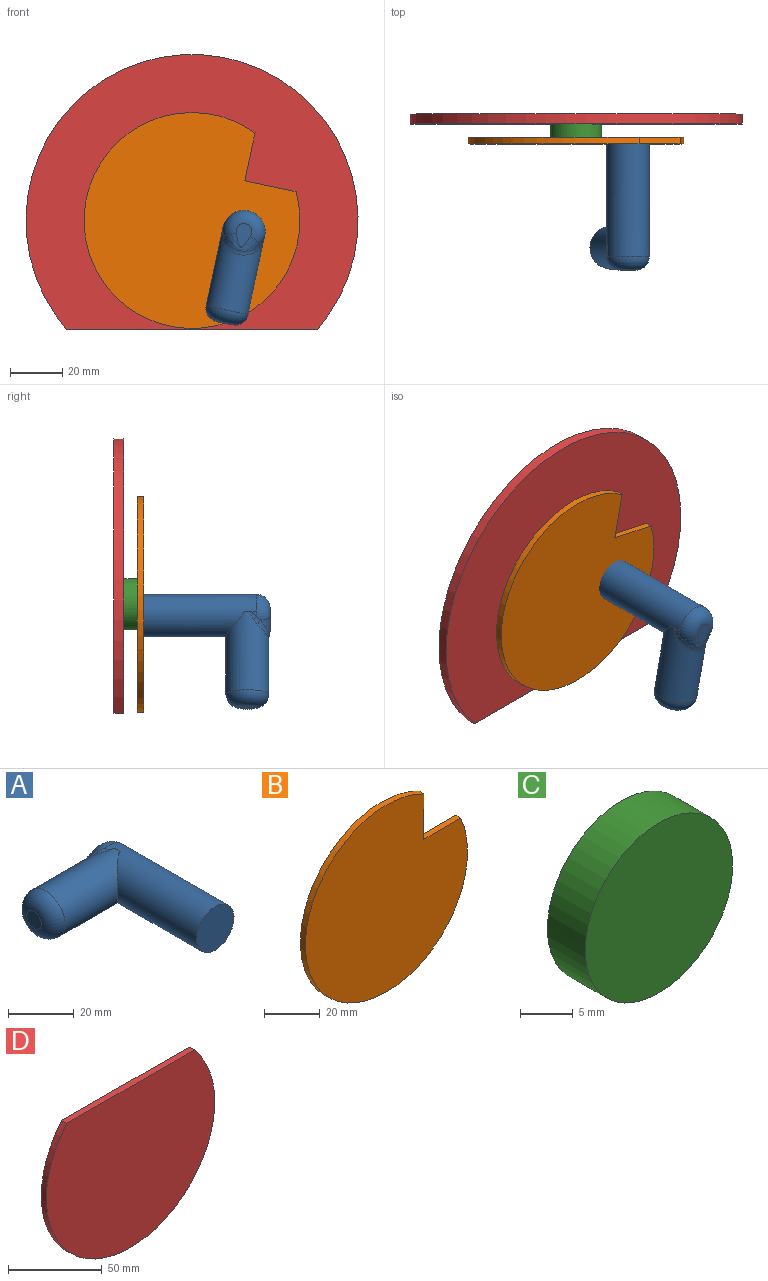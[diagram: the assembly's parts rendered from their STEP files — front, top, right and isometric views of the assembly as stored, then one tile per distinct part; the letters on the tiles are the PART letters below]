
ASSEMBLY  parts=4 mates=3
PART A: 15 faces, bbox 43.9x50.8x16.6 mm
  f0: cylinder r=8.11mm len=45.72mm, axis (0,1,0), area 2104.7mm2, adj f1,f2,f4,f5,f6,f8,f10
  f1: cylinder r=8.11mm len=1.94mm, axis (0,1,0), area 1.9mm2, adj f0,f8,f13
  f2: plane 16.22x16.22mm, normal (0,-1,0), area 206.6mm2, adj f0
  f3: plane 9.11x6.06mm, normal (0,1,0), area 37.8mm2, adj f8,f9
  f4: cylinder r=8.21mm len=30.73mm, axis (1,0,0), area 1303mm2, adj f0,f5,f6,f10,f11,f12,f13,f14
  f5: plane 2.95x0.1mm, normal (1,0,0), area 0.2mm2, adj f0,f4,f13
  f6: plane 2.6x0.1mm, normal (1,0,0), area 0.2mm2, adj f0,f4
  f7: plane 6.27x6.27mm, normal (-1,0,0), area 30.8mm2, adj f14
  f8: torus R=3.03mm, axis (0,-1,0), area 197.1mm2, adj f0,f1,f3,f9,f10,f12
  f9: bspline ~16.11x7.7mm, area 56.5mm2, adj f3,f8,f11
  f10: bspline ~5.46x3.81mm, area 6.8mm2, adj f0,f4,f8,f11
  f11: bspline ~15.04x6.45mm, area 32.1mm2, adj f4,f9,f10,f12
  f12: bspline ~4.32x3.68mm, area 4.8mm2, adj f4,f8,f11,f13
  f13: bspline ~4.16x3.21mm, area 3.5mm2, adj f1,f4,f5,f12
  f14: torus R=3.13mm, axis (1,0,0), area 319.2mm2, adj f4,f7
PART B: 5 faces, bbox 82.5x2.5x82.5 mm
  f0: plane 82.55x82.55mm, normal (0,1,0), area 5121.1mm2, adj f1,f3,f4
  f1: cylinder r=41.27mm len=82.55mm, axis (0,1,0), area 587.7mm2, adj f0,f2,f3,f4
  f2: plane 82.55x82.55mm, normal (0,-1,0), area 5121.1mm2, adj f1,f3,f4
  f3: plane 20.01x2.54mm, normal (1,0,0), area 50.8mm2, adj f0,f1,f2,f4
  f4: plane 18.72x2.54mm, normal (0,0,1), area 47.5mm2, adj f0,f1,f2,f3
PART C: 3 faces, bbox 19.8x5.1x19.8 mm
  f0: cylinder r=9.88mm len=19.76mm, axis (0,1,0), area 315.4mm2, adj f1,f2
  f1: plane 19.76x19.76mm, normal (0,-1,0), area 306.7mm2, adj f0
  f2: plane 19.76x19.76mm, normal (0,1,0), area 306.7mm2, adj f0
PART D: 4 faces, bbox 127x3.8x105.1 mm
  f0: cylinder r=63.5mm len=127mm, axis (0,1,0), area 1105.5mm2, adj f1,f2,f3
  f1: plane 127x105.08mm, normal (0,-1,0), area 11207.7mm2, adj f0,f3
  f2: plane 127x105.08mm, normal (0,1,0), area 11207.7mm2, adj f0,f3
  f3: plane 95.99x3.81mm, normal (0,0,1), area 365.7mm2, adj f0,f1,f2
PLACE A rot(axis=(0.78,0,0.63),180deg) t=(32.76,-45.43,54.32)mm
PLACE B rot(axis=(0.78,0,0.63),180deg) t=(12.89,2.83,58.56)mm
PLACE C rot(axis=(0,-1,0),180deg) t=(12.89,10.45,58.56)mm
PLACE D rot(axis=(0,-1,0),180deg) t=(12.89,14.26,58.56)mm fixed
MATE fastened C.f0 <-> D.f0  axis (0,1,0) through (12.89,10.45,58.56)mm
MATE revolute B.f1 <-> C.f0  axis (0,1,0) through (12.89,5.37,58.56)mm
MATE fastened A.f0 <-> B.f2  axis (0,1,0) through (32.76,5.37,54.32)mm
